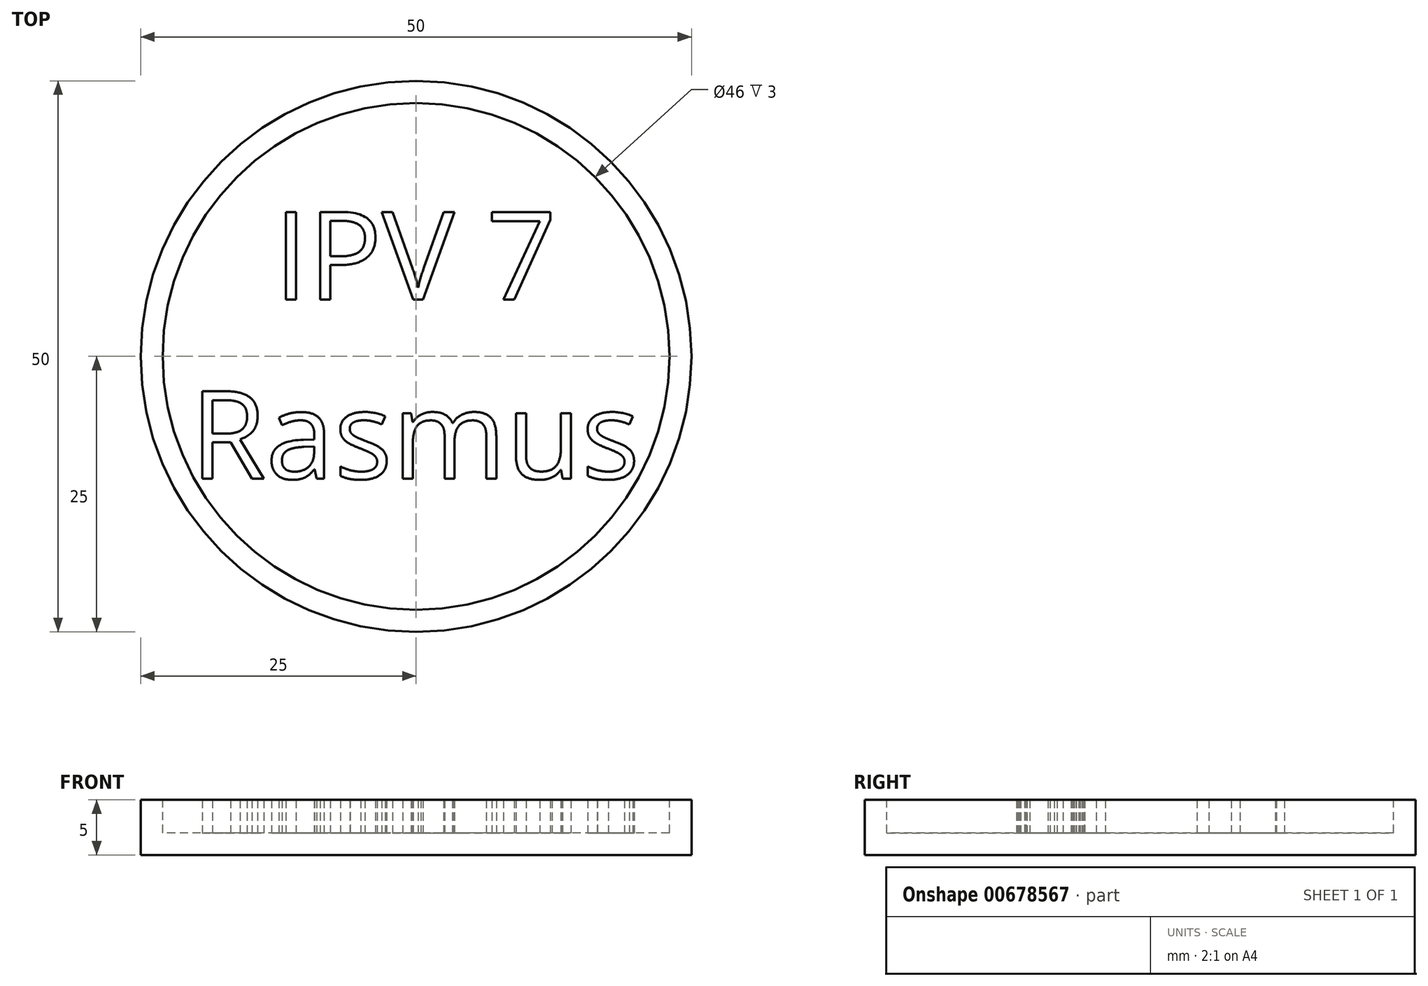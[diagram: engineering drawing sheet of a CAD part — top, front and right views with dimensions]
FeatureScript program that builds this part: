
annotation { "Feature Type Name" : "Feature", "Feature Type Description" : "" }
export const myFeature = defineFeature(function(context is Context, id is Id, definition is map)
    precondition{}
    {
        {
            var Q0;
            Q0=qCreatedBy(makeId("Front.planeOp"),FACE);
            var sketch = newSketch(context, id + "F0", { "sketchPlane" : qUnion([Q0])});
            skLineSegment(sketch, "E0", {"start": v(0, 0) * mm, "end": v(-25, 0) * mm});
            skLineSegment(sketch, "E1", {"start": v(-25, 0) * mm, "end": v(-25, 5) * mm});
            skLineSegment(sketch, "E2", {"start": v(-25, 5) * mm, "end": v(-23, 5) * mm});
            skLineSegment(sketch, "E3", {"start": v(-23, 5) * mm, "end": v(-23, 2) * mm});
            skLineSegment(sketch, "E4", {"start": v(-23, 2) * mm, "end": v(0, 2) * mm});
            skLineSegment(sketch, "E5", {"start": v(0, 2) * mm, "end": v(0, 0) * mm});
            skSolve(sketch);
        }
        {
            var Q0;
            Q0 = qSketchRegion(id + "F0", true);
            var Q1;
            Q1=sQuery(id+"F0.wireOp",EDGE,"E5");
            revolve(context, id + "F1", {"entities" : qUnion([Q0]), "axis" : qUnion([Q1]), "revolveType" : RevolveType.FULL});
        }
        {
            var Q0;
            Q0=qCreatedBy(makeId("Top.planeOp"),FACE);
            var sketch = newSketch(context, id + "F2", { "sketchPlane" : qUnion([Q0])});
            skText(sketch, "E6", { "text": "IPV 7\n", "fontName": "OpenSans-Regular.ttf"});
            const initialGuessF2  = {"E6": [-0.0129, 0.00517, 1, 0, 0.008]};
            skSetInitialGuess(sketch, initialGuessF2);
            skSolve(sketch);
        }
        {
            var Q0;
            Q0=qCreatedBy(makeId("Top.planeOp"),FACE);
            var sketch = newSketch(context, id + "F3", { "sketchPlane" : qUnion([Q0])});
            skText(sketch, "E7", { "text": "Rasmus", "fontName": "OpenSans-Regular.ttf"});
            const initialGuessF3  = {"E7": [-0.0205, -0.0111, 1, 0, 0.008]};
            skSetInitialGuess(sketch, initialGuessF3);
            skSolve(sketch);
        }
        {
            var Q0;
            Q0 = qSketchRegion(id + "F3", true);
            extrude(context, id + "F4", {"entities" : qUnion([Q0]), "operationType" : NewBodyOperationType.ADD, "depth" : 5 * mm, "offsetDistance" : 25 * mm});
        }
        {
            var Q0;
            Q0 = qSketchRegion(id + "F2", true);
            extrude(context, id + "F5", {"entities" : qUnion([Q0]), "operationType" : NewBodyOperationType.ADD, "depth" : 5 * mm, "offsetDistance" : 25 * mm});
        }
    });
